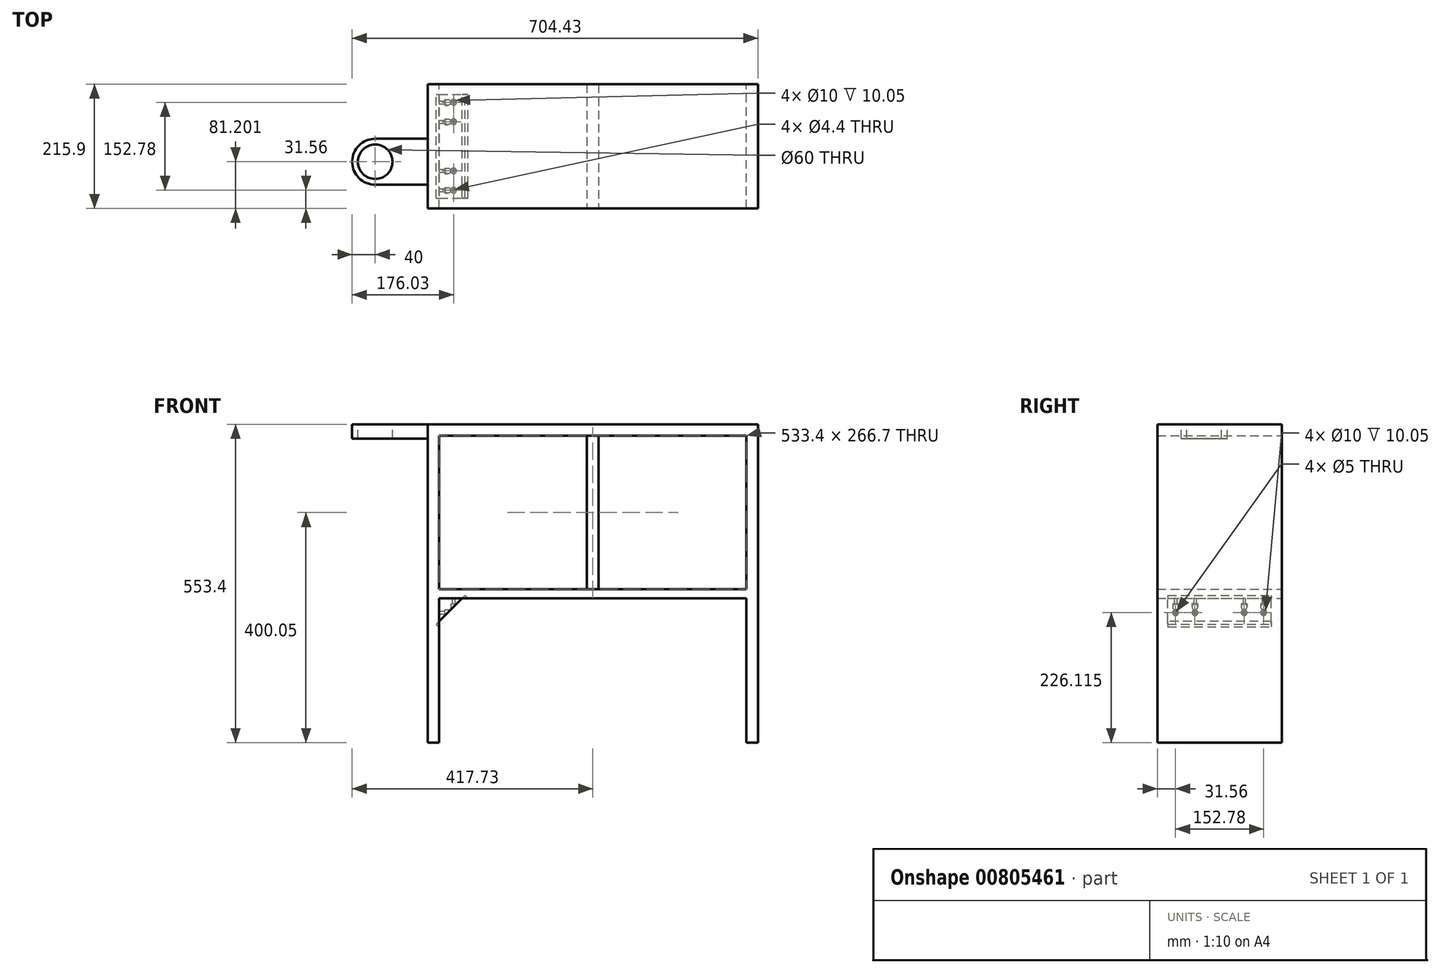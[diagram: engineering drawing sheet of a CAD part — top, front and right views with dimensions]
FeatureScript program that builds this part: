
annotation { "Feature Type Name" : "Feature", "Feature Type Description" : "" }
export const myFeature = defineFeature(function(context is Context, id is Id, definition is map)
    precondition{}
    {
        {
            var Q0;
            Q0=qCreatedBy(makeId("Front.planeOp"),FACE);
            var sketch = newSketch(context, id + "F0", { "sketchPlane" : qUnion([Q0])});
            skLineSegment(sketch, "E0.top", {"start": v(266.7, 266.7) * mm, "end": v(-266.7, 266.7) * mm});
            skLineSegment(sketch, "E0.left", {"start": v(266.7, -266.7) * mm, "end": v(266.7, -15.59) * mm});
            skLineSegment(sketch, "E0.right", {"start": v(-266.7, -266.7) * mm, "end": v(-266.7, -15.59) * mm});
            skPoint(sketch, "E0.middle", {"position": v(0, 0) * mm});
            skLineSegment(sketch, "E1.0", {"start": v(286.7, -266.7) * mm, "end": v(286.7, 286.7) * mm});
            skLineSegment(sketch, "E1.1", {"start": v(286.7, 286.7) * mm, "end": v(-286.7, 286.7) * mm});
            skLineSegment(sketch, "E1.2", {"start": v(-286.7, -266.7) * mm, "end": v(-286.7, 286.7) * mm});
            skLineSegment(sketch, "E2", {"start": v(-266.7, -15.59) * mm, "end": v(266.7, -15.59) * mm});
            skLineSegment(sketch, "E3", {"start": v(-266.7, 0) * mm, "end": v(266.7, 0) * mm});
            skLineSegment(sketch, "E4", {"start": v(-286.7, -266.7) * mm, "end": v(-266.7, -266.7) * mm});
            skLineSegment(sketch, "E5", {"start": v(266.7, -266.7) * mm, "end": v(286.7, -266.7) * mm});
            skLineSegment(sketch, "E6.trimOffspring", {"start": v(266.7, 0) * mm, "end": v(266.7, 266.7) * mm});
            skLineSegment(sketch, "E7.trimOffspring", {"start": v(-266.7, 0) * mm, "end": v(-266.7, 266.7) * mm});
            skSolve(sketch);
        }
        {
            var Q0;
            Q0=makeQuery(id+"F0.imprint","IMPRINT",FACE,{"disambiguationData":[TD([[makeQuery(id+"F0.imprint","IMPRINT",EDGE,{"derivedFrom":sQuery(id+"F0.wireOp",EDGE,"E0.top")}),-1.0]])]});
            extrude(context, id + "F1", {"entities" : qUnion([Q0]), "depth" : (8.5 * 25.4) * mm, "offsetDistance" : 25 * mm});
        }
        {
            var Q0;
            Q0=qCreatedBy(makeId("Front.planeOp"),FACE);
            cPlane(context, id + "F2", {"entities" : qUnion([Q0]), "cplaneType" : CPlaneType.OFFSET, "offset" : (25.4 * 4.25) * mm, "width" : 150 * mm, "height" : 150 * mm});
        }
        {
            var Q0;
            Q0=qCreatedBy(id+"F2.planeOp",FACE);
            var sketch = newSketch(context, id + "F3", { "sketchPlane" : qUnion([Q0])});
            skLineSegment(sketch, "E8.0", {"start": v(-266.7, -65.59) * mm, "end": v(-266.7, -15.59) * mm});
            skLineSegment(sketch, "E9.0", {"start": v(-266.7, -15.59) * mm, "end": v(-216.7, -15.59) * mm});
            skLineSegment(sketch, "E10", {"start": v(-266.7, -65.59) * mm, "end": v(-216.7, -15.59) * mm});
            skPoint(sketch, "E11.orphan", {"position": v(266.7, -15.59) * mm});
            skPoint(sketch, "E12.orphan", {"position": v(-266.7, -266.7) * mm});
            skSolve(sketch);
        }
        {
            var Q0;
            Q0=makeQuery(id+"F3.imprint","IMPRINT",FACE,{"disambiguationData":[TD([[makeQuery(id+"F3.imprint","IMPRINT",EDGE,{"derivedFrom":sQuery(id+"F3.wireOp",EDGE,"E8.0")}),-1.0]])]});
            extrude(context, id + "F4", {"entities" : qUnion([Q0]), "endBound" : BoundingType.SYMMETRIC, "depth" : 180 * mm, "offsetDistance" : 25 * mm});
        }
        {
            var Q0;
            Q0=makeQuery(id+"F4.opExtrude","SWEPT_FACE",FACE,{"disambiguationData":[OSD([sQuery(id+"F3.wireOp",EDGE,"E8.0")])]});
            cPlane(context, id + "F5", {"entities" : qUnion([Q0]), "cplaneType" : CPlaneType.OFFSET, "offset" : 40 * mm, "oppositeDirection" : true, "width" : 150 * mm, "height" : 150 * mm});
        }
        {
            var Q0;
            Q0=qCreatedBy(id+"F5.planeOp",FACE);
            var sketch = newSketch(context, id + "F6", { "sketchPlane" : qUnion([Q0])});
            skPoint(sketch, "E13.0", {"position": v(197.95, -40.59) * mm});
            skPoint(sketch, "E14.0", {"position": v(17.95, -40.59) * mm});
            skLineSegment(sketch, "E15", {"start": v(197.95, -40.59) * mm, "end": v(17.95, -40.59) * mm});
            skPoint(sketch, "E16", {"position": v(184.34, -40.59) * mm});
            skPoint(sketch, "E17", {"position": v(150.7, -40.59) * mm});
            skPoint(sketch, "E18.MirrorP", {"position": v(31.56, -40.59) * mm});
            skPoint(sketch, "E19.MirrorP", {"position": v(65.2, -40.59) * mm});
            skSolve(sketch);
        }
        {
            var Q0;
            Q0=makeQuery(id+"F4.opExtrude","SWEPT_FACE",FACE,{"disambiguationData":[OSD([sQuery(id+"F3.wireOp",EDGE,"E9.0")])]});
            cPlane(context, id + "F7", {"entities" : qUnion([Q0]), "cplaneType" : CPlaneType.OFFSET, "offset" : 40 * mm, "oppositeDirection" : true, "width" : 150 * mm, "height" : 150 * mm});
        }
        {
            var Q0;
            Q0=qCreatedBy(id+"F7.planeOp",FACE);
            var sketch = newSketch(context, id + "F8", { "sketchPlane" : qUnion([Q0])});
            skPoint(sketch, "E20.0", {"position": v(-241.7, -184.34) * mm});
            skPoint(sketch, "E21.0", {"position": v(-241.7, -150.7) * mm});
            skPoint(sketch, "E22.0", {"position": v(-241.7, -65.2) * mm});
            skPoint(sketch, "E23.0", {"position": v(-241.7, -31.56) * mm});
            skSolve(sketch);
        }
        {
            var Q0;
            Q0=sQuery(id+"F6.wireOp",VERTEX,"E16");
            var Q1;
            Q1=sQuery(id+"F6.wireOp",VERTEX,"E17");
            var Q2;
            Q2=sQuery(id+"F6.wireOp",VERTEX,"E19.MirrorP");
            var Q3;
            Q3=sQuery(id+"F6.wireOp",VERTEX,"E18.MirrorP");
            var Q4;
            Q4=makeQuery(id+"F4.opExtrude","SWEPT_BODY",BODY,{"disambiguationData":[OSD([sQuery(id+"F3.wireOp",EDGE,"E8.0"),sQuery(id+"F3.wireOp",EDGE,"E9.0"),sQuery(id+"F3.wireOp",EDGE,"E10")])]});
            hole(context, id + "F9", {"style" : HoleStyle.C_BORE, "endStyle" : HoleEndStyle.BLIND, "oppositeDirection" : true, "holeDiameter" : 5 * mm, "cBoreDiameter" : 10 * mm, "cBoreDepth" : 30 * mm, "majorDiameter" : 5 * mm, "holeDepth" : 70 * mm, "isTappedThrough" : true, "tappedDepth" : 12 * mm, "tapClearance" : 3, "startFromSketch" : true, "locations" : qUnion([Q0, Q1, Q2, Q3]), "scope" : qUnion([Q4])});
        }
        {
            var Q0;
            Q0=sQuery(id+"F8.wireOp",VERTEX,"E20.0");
            var Q1;
            Q1=sQuery(id+"F8.wireOp",VERTEX,"E21.0");
            var Q2;
            Q2=sQuery(id+"F8.wireOp",VERTEX,"E22.0");
            var Q3;
            Q3=sQuery(id+"F8.wireOp",VERTEX,"E23.0");
            var Q4;
            Q4=makeQuery(id+"F4.opExtrude","SWEPT_BODY",BODY,{"disambiguationData":[OSD([sQuery(id+"F3.wireOp",EDGE,"E8.0"),sQuery(id+"F3.wireOp",EDGE,"E9.0"),sQuery(id+"F3.wireOp",EDGE,"E10")])]});
            hole(context, id + "F10", {"style" : HoleStyle.C_BORE, "endStyle" : HoleEndStyle.BLIND, "oppositeDirection" : true, "holeDiameter" : 4.4 * mm, "cBoreDiameter" : 10 * mm, "cBoreDepth" : 30 * mm, "majorDiameter" : 5 * mm, "holeDepth" : 70 * mm, "isTappedThrough" : true, "tappedDepth" : 12 * mm, "tapClearance" : 3, "startFromSketch" : true, "locations" : qUnion([Q0, Q1, Q2, Q3]), "scope" : qUnion([Q4])});
        }
        {
            var Q0;
            Q0=makeQuery(id+"F1.opExtrude","SWEPT_FACE",FACE,{"disambiguationData":[OSD([sQuery(id+"F0.wireOp",EDGE,"E0.top")])]});
            var sketch = newSketch(context, id + "F11", { "sketchPlane" : qUnion([Q0])});
            skLineSegment(sketch, "E24.0", {"start": v(-10, 215.9) * mm, "end": v(-10, 0) * mm});
            skLineSegment(sketch, "E25.0", {"start": v(10, 215.9) * mm, "end": v(10, 0) * mm});
            skPoint(sketch, "E26.end.orphan", {"position": v(0, 0) * mm});
            skPoint(sketch, "E26.start.orphan", {"position": v(0, 215.9) * mm});
            skLineSegment(sketch, "E27", {"start": v(-10, 215.9) * mm, "end": v(10, 215.9) * mm});
            skLineSegment(sketch, "E28", {"start": v(-10, 0) * mm, "end": v(10, 0) * mm});
            skSolve(sketch);
        }
        {
            var Q0;
            Q0=makeQuery(id+"F11.imprint","IMPRINT",FACE,{"disambiguationData":[TD([[makeQuery(id+"F11.imprint","IMPRINT",EDGE,{"derivedFrom":sQuery(id+"F11.wireOp",EDGE,"E24.0")}),1.0]])]});
            var Q1;
            Q1=makeQuery(id+"F1.opExtrude","SWEPT_FACE",FACE,{"disambiguationData":[OSD([sQuery(id+"F0.wireOp",EDGE,"E3")])]});
            extrude(context, id + "F12", {"entities" : qUnion([Q0]), "endBound" : BoundingType.UP_TO_SURFACE, "depth" : 25 * mm, "endBoundEntityFace" : qUnion([Q1]), "offsetDistance" : 25 * mm});
        }
        {
            var Q0;
            Q0=makeQuery(id+"F1.opExtrude","SWEPT_FACE",FACE,{"disambiguationData":[OSD([sQuery(id+"F0.wireOp",EDGE,"E1.1")])]});
            var sketch = newSketch(context, id + "F13", { "sketchPlane" : qUnion([Q0])});
            skLineSegment(sketch, "E29", {"start": v(-286.7, -94.7) * mm, "end": v(-286.7, -174.7) * mm});
            skLineSegment(sketch, "E30", {"start": v(-286.7, -94.7) * mm, "end": v(-377.73, -94.7) * mm});
            skLineSegment(sketch, "E31", {"start": v(-286.7, -174.7) * mm, "end": v(-377.73, -174.7) * mm});
            skArc(sketch, "E32", {"start": v(-377.73, -94.7) * mm, "mid": v(-417.73, -134.7) * mm, "end": v(-377.73, -174.7) * mm});
            skCircle(sketch, "E33", {"center": v(-377.73, -134.7) * mm, "radius": 30 * mm});
            skSolve(sketch);
        }
        {
            var Q0;
            Q0=makeQuery(id+"F13.imprint","IMPRINT",FACE,{"disambiguationData":[TD([[makeQuery(id+"F13.imprint","IMPRINT",EDGE,{"derivedFrom":sQuery(id+"F13.wireOp",EDGE,"E29")}),1.0]])]});
            extrude(context, id + "F14", {"entities" : qUnion([Q0]), "oppositeDirection" : true, "depth" : 25 * mm, "offsetDistance" : 25 * mm});
        }
        {
            var Q0;
            Q0=makeQuery(id+"F4.opExtrude","SWEPT_FACE",FACE,{"disambiguationData":[OSD([sQuery(id+"F3.wireOp",EDGE,"E10")])]});
            var sketch = newSketch(context, id + "F15", { "sketchPlane" : qUnion([Q0])});
            skLineSegment(sketch, "E34.0", {"start": v(-197.95, -234.96) * mm, "end": v(-197.95, -164.25) * mm});
            skLineSegment(sketch, "E35.0", {"start": v(-197.95, -164.25) * mm, "end": v(-17.95, -164.25) * mm});
            skLineSegment(sketch, "E36.0", {"start": v(-197.95, -234.96) * mm, "end": v(-17.95, -234.96) * mm});
            skLineSegment(sketch, "E37.0", {"start": v(-17.95, -234.96) * mm, "end": v(-17.95, -164.25) * mm});
            skSolve(sketch);
        }
        {
            var Q0;
            Q0 = qSketchRegion(id + "F15", true);
            extrude(context, id + "F16", {"entities" : qUnion([Q0]), "operationType" : NewBodyOperationType.REMOVE, "oppositeDirection" : true, "depth" : 7 * mm, "offsetDistance" : 25 * mm});
        }
    });
